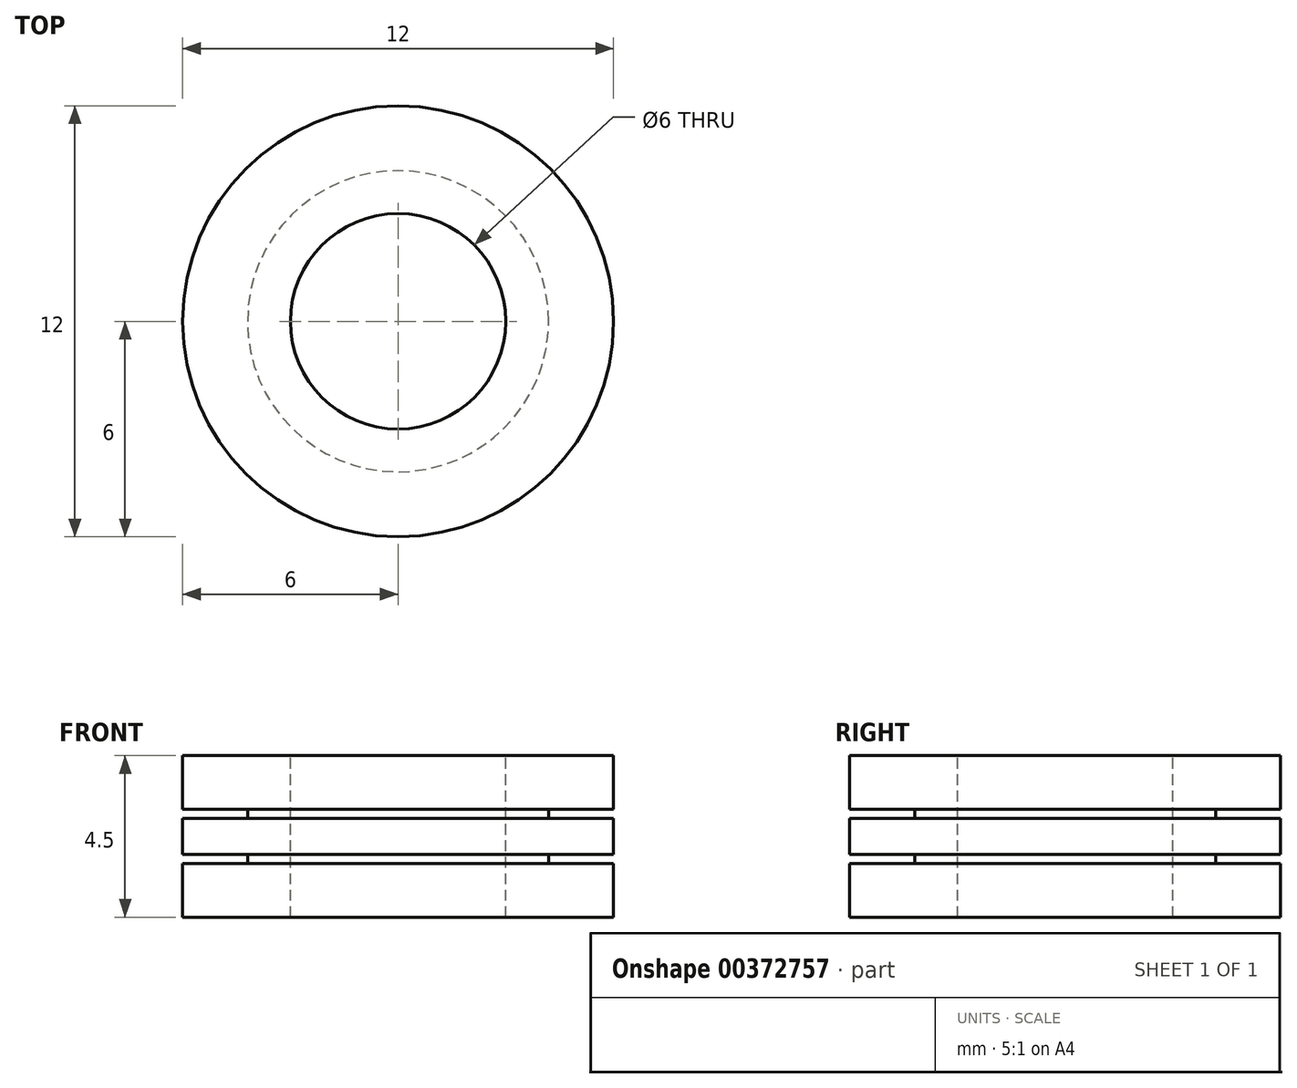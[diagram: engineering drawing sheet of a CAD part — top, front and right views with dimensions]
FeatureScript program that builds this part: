
annotation { "Feature Type Name" : "Feature", "Feature Type Description" : "" }
export const myFeature = defineFeature(function(context is Context, id is Id, definition is map)
    precondition{}
    {
        {
            var Q0;
            Q0=qCreatedBy(makeId("Front.planeOp"),FACE);
            var sketch = newSketch(context, id + "F0", { "sketchPlane" : qUnion([Q0])});
            skLineSegment(sketch, "E0", {"start": v(0, 2.68) * mm, "end": v(0, -3.7) * mm, "construction": true});
            skLineSegment(sketch, "E1", {"start": v(3, 2.25) * mm, "end": v(6, 2.25) * mm});
            skLineSegment(sketch, "E2", {"start": v(6, 2.25) * mm, "end": v(6, 0.75) * mm});
            skLineSegment(sketch, "E3", {"start": v(6, 0.75) * mm, "end": v(4.2, 0.75) * mm});
            skLineSegment(sketch, "E4", {"start": v(4.2, 0.75) * mm, "end": v(4.2, 0.5) * mm});
            skLineSegment(sketch, "E5", {"start": v(4.2, 0.5) * mm, "end": v(6, 0.5) * mm});
            skLineSegment(sketch, "E6", {"start": v(6, 0.5) * mm, "end": v(6, -0.5) * mm});
            skLineSegment(sketch, "E7", {"start": v(6, -0.5) * mm, "end": v(4.2, -0.5) * mm});
            skLineSegment(sketch, "E8", {"start": v(4.2, -0.5) * mm, "end": v(4.2, -0.75) * mm});
            skLineSegment(sketch, "E9", {"start": v(4.2, -0.75) * mm, "end": v(6, -0.75) * mm});
            skLineSegment(sketch, "E10", {"start": v(6, -0.75) * mm, "end": v(6, -2.25) * mm});
            skLineSegment(sketch, "E11", {"start": v(6, -2.25) * mm, "end": v(3, -2.25) * mm});
            skLineSegment(sketch, "E12", {"start": v(3, -2.25) * mm, "end": v(3, 2.25) * mm});
            skLineSegment(sketch, "E13", {"start": v(-0.99, 0) * mm, "end": v(6.42, 0) * mm, "construction": true});
            skSolve(sketch);
        }
        {
            var Q0;
            Q0 = qSketchRegion(id + "F0", true);
            var Q1;
            Q1=sQuery(id+"F0.wireOp",EDGE,"E0");
            revolve(context, id + "F1", {"surfaceOperationType" : NewSurfaceOperationType.NEW, "entities" : qUnion([Q0]), "axis" : qUnion([Q1]), "revolveType" : RevolveType.FULL});
        }
    });
